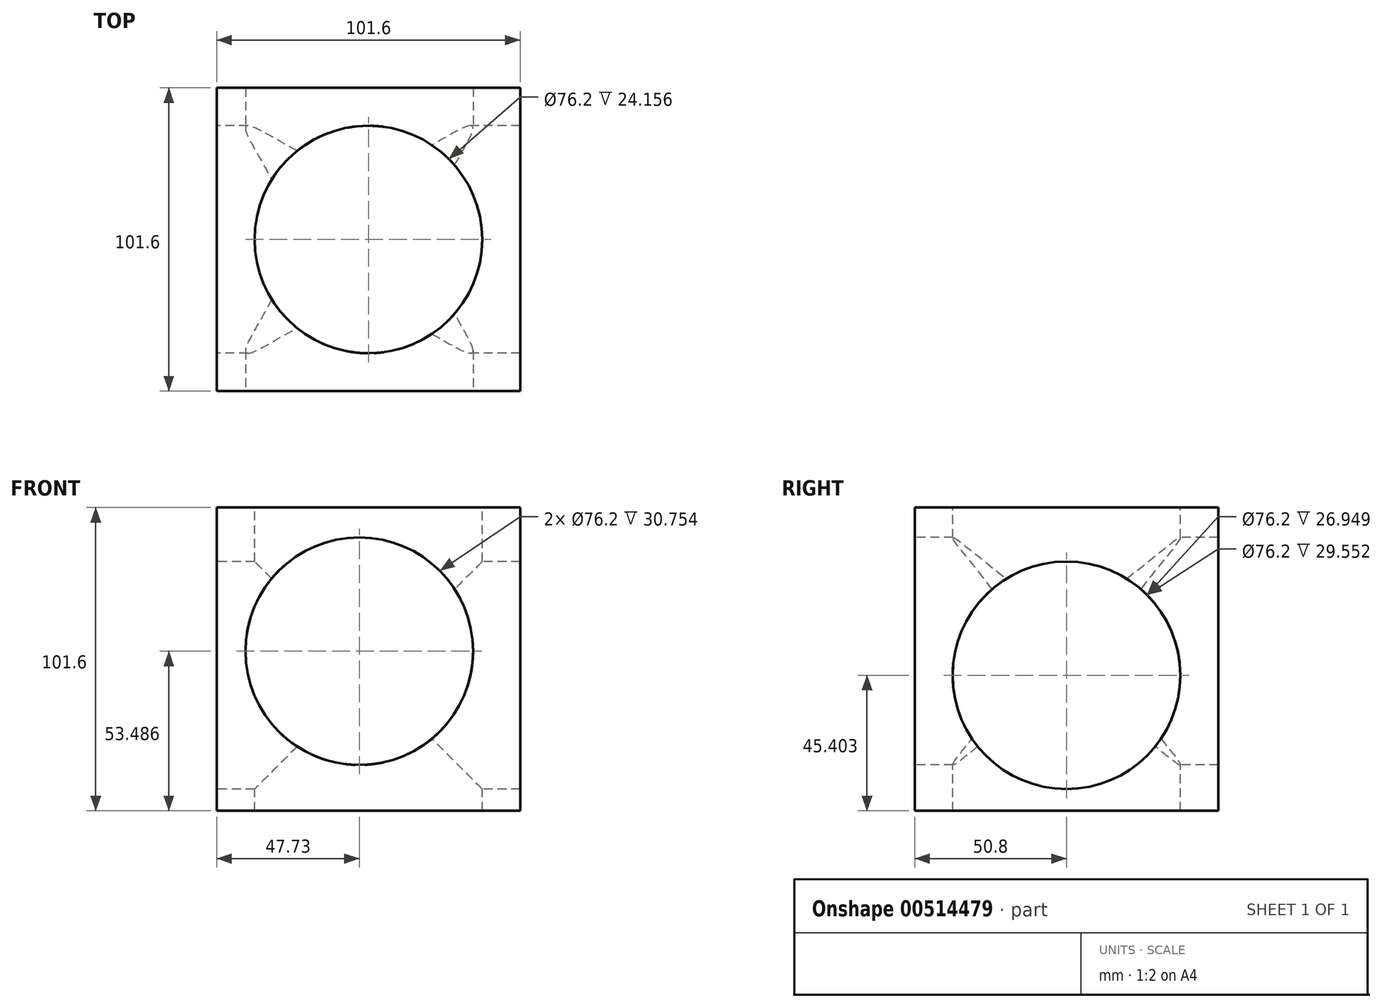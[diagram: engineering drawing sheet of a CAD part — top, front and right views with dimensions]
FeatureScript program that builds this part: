
annotation { "Feature Type Name" : "Feature", "Feature Type Description" : "" }
export const myFeature = defineFeature(function(context is Context, id is Id, definition is map)
    precondition{}
    {
        {
            var Q0;
            Q0=qCreatedBy(makeId("Top.planeOp"),FACE);
            var sketch = newSketch(context, id + "F0", { "sketchPlane" : qUnion([Q0])});
            skLineSegment(sketch, "E0.bottom", {"start": v(50.8, -50.8) * mm, "end": v(-50.8, -50.8) * mm});
            skLineSegment(sketch, "E0.top", {"start": v(50.8, 50.8) * mm, "end": v(-50.8, 50.8) * mm});
            skLineSegment(sketch, "E0.left", {"start": v(50.8, -50.8) * mm, "end": v(50.8, 50.8) * mm});
            skLineSegment(sketch, "E0.right", {"start": v(-50.8, -50.8) * mm, "end": v(-50.8, 50.8) * mm});
            skPoint(sketch, "E0.middle", {"position": v(0, 0) * mm});
            skPoint(sketch, "E1.4.internal.orphan", {"position": v(0, 6.31) * mm});
            skSolve(sketch);
        }
        {
            var Q0;
            Q0=makeQuery(id+"F0.imprint","IMPRINT",FACE,{"disambiguationData":[TD([[makeQuery(id+"F0.imprint","IMPRINT",EDGE,{"derivedFrom":sQuery(id+"F0.wireOp",EDGE,"E0.bottom")}),-1.0]])]});
            extrude(context, id + "F1", {"entities" : qUnion([Q0]), "depth" : 101.6 * mm});
        }
        {
            var Q0;
            Q0=makeQuery(id+"F1.opExtrude","CAP_FACE",FACE,{"disambiguationData":[OSD([sQuery(id+"F0.wireOp",EDGE,"E0.bottom"),sQuery(id+"F0.wireOp",EDGE,"E0.top"),sQuery(id+"F0.wireOp",EDGE,"E0.left"),sQuery(id+"F0.wireOp",EDGE,"E0.right")])],"isStart":false});
            var sketch = newSketch(context, id + "F2", { "sketchPlane" : qUnion([Q0])});
            skCircle(sketch, "E2", {"center": v(0, 0) * mm, "radius": 38.1 * mm});
            skSolve(sketch);
        }
        {
            var Q0;
            Q0=makeQuery(id+"F2.imprint","IMPRINT",FACE,{"disambiguationData":[TD([[makeQuery(id+"F2.imprint","IMPRINT",EDGE,{"derivedFrom":sQuery(id+"F2.wireOp",EDGE,"E2")}),1.0]])]});
            extrude(context, id + "F3", {"entities" : qUnion([Q0]), "operationType" : NewBodyOperationType.REMOVE, "oppositeDirection" : true, "depth" : 101.6 * mm});
        }
        {
            var Q0;
            Q0=makeQuery(id+"F1.opExtrude","SWEPT_FACE",FACE,{"disambiguationData":[OSD([sQuery(id+"F0.wireOp",EDGE,"E0.bottom")])]});
            var sketch = newSketch(context, id + "F4", { "sketchPlane" : qUnion([Q0])});
            skSolve(sketch);
        }
        {
            var Q0;
            Q0=makeQuery(id+"F1.opExtrude","SWEPT_FACE",FACE,{"disambiguationData":[OSD([sQuery(id+"F0.wireOp",EDGE,"E0.right")])]});
            var sketch = newSketch(context, id + "F5", { "sketchPlane" : qUnion([Q0])});
            skCircle(sketch, "E3", {"center": v(0, 45.4) * mm, "radius": 38.1 * mm});
            skSolve(sketch);
        }
        {
            var Q0;
            Q0 = qSketchRegion(id + "F5", true);
            extrude(context, id + "F6", {"entities" : qUnion([Q0]), "operationType" : NewBodyOperationType.REMOVE, "oppositeDirection" : true, "depth" : 101.6 * mm});
        }
        {
            var Q0;
            {var subQ0=sQuery(id+"F0.wireOp",EDGE,"E0.bottom");Q0=makeQuery(id+"F4.imprint","IMPRINT",FACE,{"disambiguationData":[TD([[makeQuery(id+"F4.imprint","IMPRINT",EDGE,{"derivedFrom":makeQuery(id+"F1.opExtrude","CAP_EDGE",EDGE,{"disambiguationData":[OSD([subQ0])],"isStart":true})}),-1.0]])]});}
            var sketch = newSketch(context, id + "F7", { "sketchPlane" : qUnion([Q0])});
            skCircle(sketch, "E4", {"center": v(-3.07, 53.49) * mm, "radius": 38.1 * mm});
            skSolve(sketch);
        }
        {
            var Q0;
            Q0 = qSketchRegion(id + "F7", true);
            extrude(context, id + "F8", {"entities" : qUnion([Q0]), "operationType" : NewBodyOperationType.REMOVE, "depth" : 101.6 * mm});
        }
        {
            var Q0;
            Q0=makeQuery(id+"F7.imprint","IMPRINT",FACE,{"disambiguationData":[TD([[makeQuery(id+"F7.imprint","IMPRINT",EDGE,{"derivedFrom":sQuery(id+"F7.wireOp",EDGE,"E4")}),1.0]])]});
            extrude(context, id + "F9", {"entities" : qUnion([Q0]), "operationType" : NewBodyOperationType.REMOVE, "oppositeDirection" : true, "depth" : 101.6 * mm});
        }
    });
